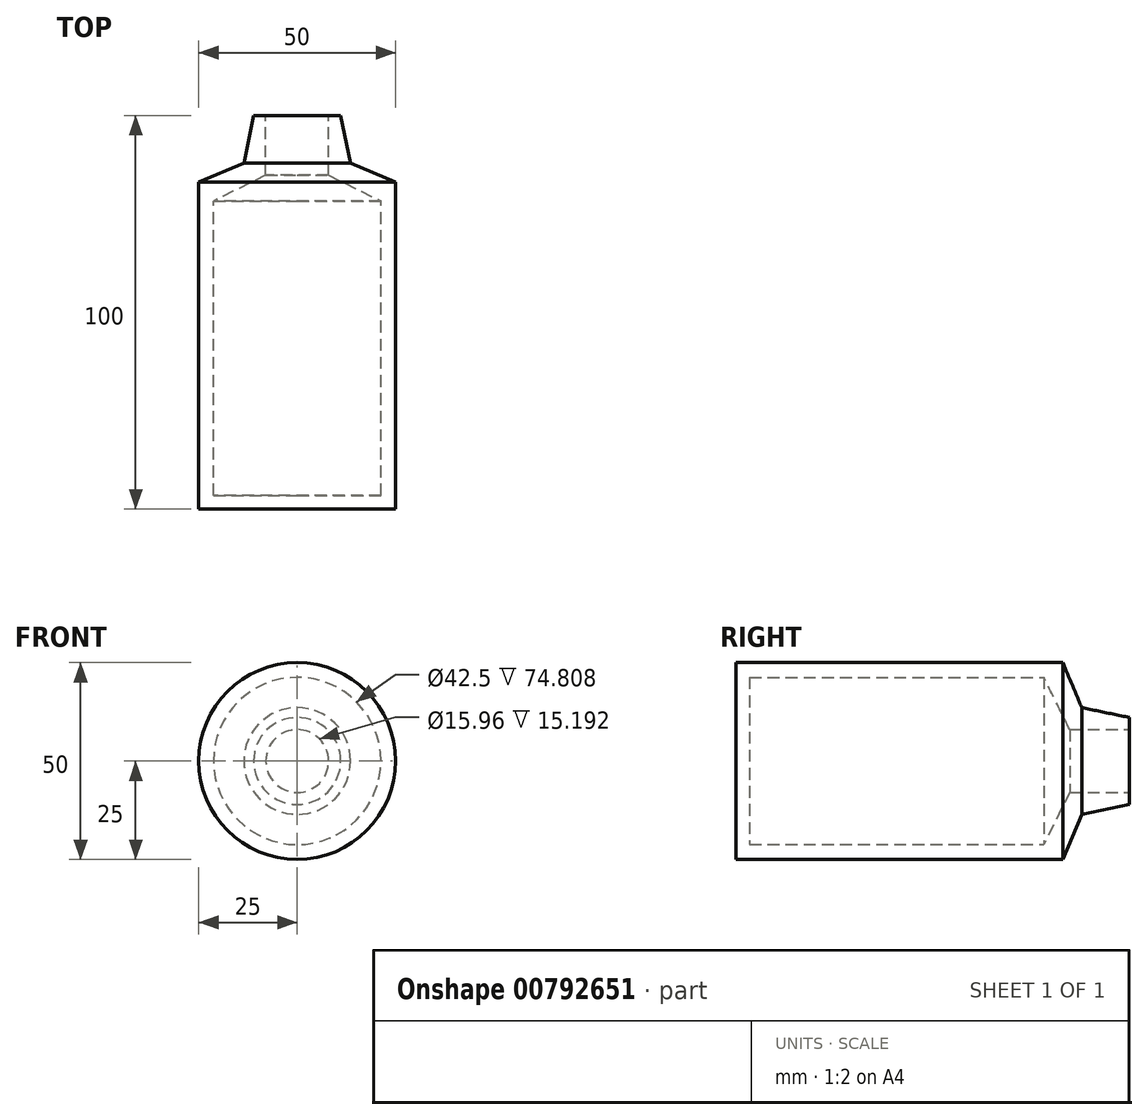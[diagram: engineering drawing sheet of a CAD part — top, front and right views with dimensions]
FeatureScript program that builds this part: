
annotation { "Feature Type Name" : "Feature", "Feature Type Description" : "" }
export const myFeature = defineFeature(function(context is Context, id is Id, definition is map)
    precondition{}
    {
        {
            var Q0;
            Q0=qCreatedBy(makeId("Top.planeOp"),FACE);
            var sketch = newSketch(context, id + "F0", { "sketchPlane" : qUnion([Q0])});
            skLineSegment(sketch, "E0.bottom", {"start": v(25, -50) * mm, "end": v(-25, -50) * mm});
            skLineSegment(sketch, "E0.top", {"start": v(11.06, 50) * mm, "end": v(7.98, 50) * mm});
            skLineSegment(sketch, "E0.left", {"start": v(25, -50) * mm, "end": v(25, 33.08) * mm});
            skLineSegment(sketch, "E0.right", {"start": v(-25, -50) * mm, "end": v(-25, 33.08) * mm});
            skPoint(sketch, "E0.middle", {"position": v(0, 0) * mm});
            skLineSegment(sketch, "E1", {"start": v(-11.06, 50) * mm, "end": v(-13.56, 37.88) * mm});
            skLineSegment(sketch, "E2", {"start": v(-13.56, 37.88) * mm, "end": v(-25, 33.08) * mm});
            skLineSegment(sketch, "E3.MirrorCS", {"start": v(11.06, 50) * mm, "end": v(13.56, 37.88) * mm});
            skLineSegment(sketch, "E4.MirrorCS", {"start": v(13.56, 37.88) * mm, "end": v(25, 33.08) * mm});
            skPoint(sketch, "E5.orphan", {"position": v(-25, 50) * mm});
            skPoint(sketch, "E6.orphan", {"position": v(25, 50) * mm});
            skLineSegment(sketch, "E7", {"start": v(-7.98, 50) * mm, "end": v(-7.98, 34.8) * mm});
            skLineSegment(sketch, "E8", {"start": v(-7.98, 34.8) * mm, "end": v(-21.25, 28.27) * mm});
            skLineSegment(sketch, "E9", {"start": v(-21.25, 28.27) * mm, "end": v(-21.25, -46.54) * mm});
            skLineSegment(sketch, "E10.MirrorCS", {"start": v(7.98, 50) * mm, "end": v(7.98, 34.8) * mm});
            skLineSegment(sketch, "E11.MirrorCS", {"start": v(7.98, 34.8) * mm, "end": v(21.25, 28.27) * mm});
            skLineSegment(sketch, "E12.MirrorCS", {"start": v(21.25, 28.27) * mm, "end": v(21.25, -46.54) * mm});
            skLineSegment(sketch, "E13", {"start": v(-21.25, -46.54) * mm, "end": v(0, -46.54) * mm});
            skLineSegment(sketch, "E14.MirrorCS", {"start": v(21.25, -46.54) * mm, "end": v(0, -46.54) * mm});
            skLineSegment(sketch, "E15.trimOffspring", {"start": v(-7.98, 50) * mm, "end": v(-11.06, 50) * mm});
            skLineSegment(sketch, "E16", {"start": v(0, 67.12) * mm, "end": v(0, -61.54) * mm});
            skSolve(sketch);
        }
        {
            var Q0;
            {var subQ0=sQuery(id+"F0.wireOp",EDGE,"E0.right");Q0=makeQuery(id+"F0.imprint","IMPRINT",FACE,{"disambiguationData":[TD([[makeQuery(id+"F0.imprint","IMPRINT",EDGE,{"derivedFrom":subQ0}),-1.0]])]});}
            var Q1;
            Q1=sQuery(id+"F0.wireOp",EDGE,"E16");
            revolve(context, id + "F1", {"surfaceOperationType" : NewSurfaceOperationType.NEW, "entities" : qUnion([Q0]), "axis" : qUnion([Q1]), "revolveType" : RevolveType.FULL});
        }
    });
